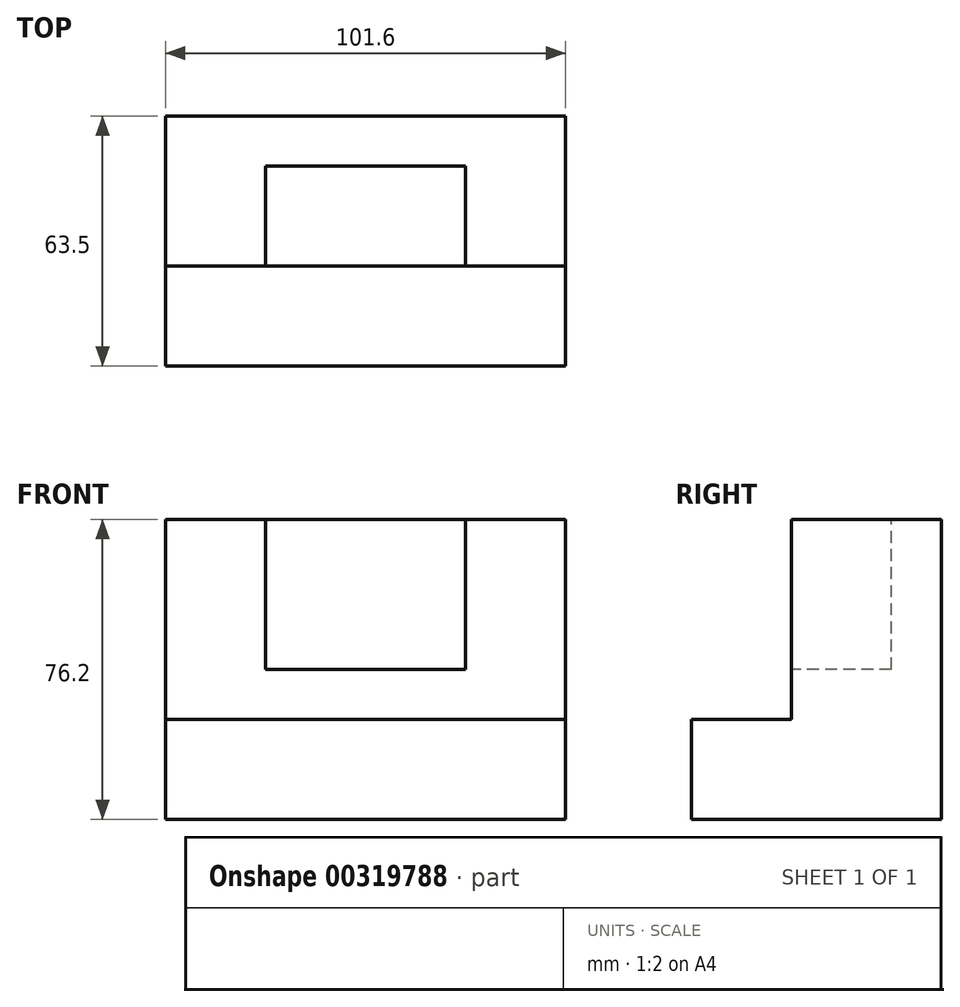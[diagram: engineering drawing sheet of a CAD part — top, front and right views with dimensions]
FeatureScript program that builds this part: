
annotation { "Feature Type Name" : "Feature", "Feature Type Description" : "" }
export const myFeature = defineFeature(function(context is Context, id is Id, definition is map)
    precondition{}
    {
        {
            var Q0;
            Q0=qCreatedBy(makeId("Right.planeOp"),FACE);
            var sketch = newSketch(context, id + "F0", { "sketchPlane" : qUnion([Q0])});
            skLineSegment(sketch, "E0", {"start": v(-37.87, -46.88) * mm, "end": v(-37.87, -21.48) * mm});
            skLineSegment(sketch, "E1", {"start": v(-37.87, -21.48) * mm, "end": v(-12.47, -21.48) * mm});
            skLineSegment(sketch, "E2", {"start": v(-12.47, -21.48) * mm, "end": v(-12.47, 29.32) * mm});
            skLineSegment(sketch, "E3", {"start": v(-12.47, 29.32) * mm, "end": v(25.63, 29.32) * mm});
            skLineSegment(sketch, "E4", {"start": v(25.63, 29.32) * mm, "end": v(25.63, -46.88) * mm});
            skLineSegment(sketch, "E5", {"start": v(25.63, -46.88) * mm, "end": v(-37.87, -46.88) * mm});
            skSolve(sketch);
        }
        {
            var Q0;
            Q0=makeQuery(id+"F0.imprint","IMPRINT",FACE,{"disambiguationData":[TD([[makeQuery(id+"F0.imprint","IMPRINT",EDGE,{"derivedFrom":sQuery(id+"F0.wireOp",EDGE,"E0")}),-1.0]])]});
            extrude(context, id + "F1", {"entities" : qUnion([Q0]), "oppositeDirection" : true, "depth" : 101.6 * mm});
        }
        {
            var Q0;
            Q0=makeQuery(id+"F1.opExtrude","SWEPT_FACE",FACE,{"disambiguationData":[OSD([sQuery(id+"F0.wireOp",EDGE,"E2")])]});
            var sketch = newSketch(context, id + "F2", { "sketchPlane" : qUnion([Q0])});
            skLineSegment(sketch, "E6", {"start": v(-76.2, -8.78) * mm, "end": v(-25.4, -8.78) * mm});
            skLineSegment(sketch, "E7", {"start": v(-25.4, -8.78) * mm, "end": v(-25.4, 29.32) * mm});
            skLineSegment(sketch, "E8", {"start": v(-76.2, -8.78) * mm, "end": v(-76.2, 29.32) * mm});
            skSolve(sketch);
        }
        {
            var Q0;
            Q0=makeQuery(id+"F2.imprint","IMPRINT",FACE,{"disambiguationData":[TD([[makeQuery(id+"F2.imprint","IMPRINT",EDGE,{"derivedFrom":sQuery(id+"F2.wireOp",EDGE,"E6")}),1.0]])]});
            extrude(context, id + "F3", {"entities" : qUnion([Q0]), "operationType" : NewBodyOperationType.REMOVE, "oppositeDirection" : true, "depth" : 25.4 * mm});
        }
    });
